FCSTD DOCUMENT  (FreeCAD 0.20R29177 (Git))
Label: AT_900a_GA3Dtech_M1_assembly
License: All rights reserved
LicenseURL: http://en.wikipedia.org/wiki/All_rights_reserved
objects: App::FeaturePython×56, Part::FeaturePython×13, PartDesign::ShapeBinder×6, Sketcher::SketchObject×2, PartDesign::Body×2, PartDesign::AdditivePipe×1, PartDesign::FeatureBase×1
note: 26 computed .brp shape members not serialized (recipe doc carries the construction recipe); baked Part::Feature solids carry a one-line shape summary decoded from their .brp

FEATURE [Part::FeaturePython] b_AQ_901b_Frame_001_  label="AQ_901b_Frame_001"  # a2plus imported part (geometry in sourceFile) (typed FeaturePython)
  a2p_Version = V0.1
  fixedPosition = true
  objectType = a2pPart
  sourceFile = ./AQ_901b_Frame.FCStd
  subassemblyImport = true
  timeLastImport = 1656490796
  updateColors = true
FEATURE [Part::FeaturePython] b_AT_912a_Yaxis_001_  label="AT_912a_Yaxis_001"  # a2plus imported part (geometry in sourceFile) (typed FeaturePython)
  Placement = pos=(100.718,28,161.125) rot=(0,0,1;0rad)
  a2p_Version = V0.1
  fixedPosition = false
  objectType = a2pPart
  sourceFile = ./AT_912a_Yaxis.FCStd
  subassemblyImport = true
  timeLastImport = 1656492010
  updateColors = true
FEATURE [App::FeaturePython] planeCoincident_001  label="planeCoincident_001__AQ_901b_Frame_001"  # a2plus constraint (typed FeaturePython)
  Object1 = b_AT_912a_Yaxis_001_
  Object2 = b_AQ_901b_Frame_001_
  ParentTreeObject = -> b_AT_912a_Yaxis_001_
  SubElement1 = Face1710
  SubElement2 = Face101
  Suppressed = false
  Type = plane
  directionConstraint = 1
  offset = 0
FEATURE [App::FeaturePython] planeCoincident_001_mirror  label="planeCoincident_001__AT_912a_Yaxis_001"  # a2plus constraint (typed FeaturePython)
  Object1 = b_AT_912a_Yaxis_001_
  Object2 = b_AQ_901b_Frame_001_
  ParentTreeObject = -> b_AQ_901b_Frame_001_
  SubElement1 = Face1710
  SubElement2 = Face101
  Suppressed = false
  Type = plane
  directionConstraint = 1
  offset = 0
FEATURE [App::FeaturePython] planeCoincident_002  label="planeCoincident_002__AT_912a_Yaxis_001"  # a2plus constraint (typed FeaturePython)
  Object1 = b_AQ_901b_Frame_001_
  Object2 = b_AT_912a_Yaxis_001_
  ParentTreeObject = -> b_AQ_901b_Frame_001_
  SubElement1 = Face99
  SubElement2 = Face1479
  Suppressed = false
  Type = plane
  directionConstraint = 1
  offset = 6
FEATURE [App::FeaturePython] planeCoincident_002_mirror  label="planeCoincident_002__AQ_901b_Frame_001"  # a2plus constraint (typed FeaturePython)
  Object1 = b_AQ_901b_Frame_001_
  Object2 = b_AT_912a_Yaxis_001_
  ParentTreeObject = -> b_AT_912a_Yaxis_001_
  SubElement1 = Face99
  SubElement2 = Face1479
  Suppressed = false
  Type = plane
  directionConstraint = 1
  offset = 6
FEATURE [Part::FeaturePython] b_AP_982a_DoubleFrontBlocAssembly_001_  label="AP_982a_DoubleFrontBlocAssembly_001"  # a2plus imported part (geometry in sourceFile) (typed FeaturePython)
  Placement = pos=(135.2,436.271,236.375) rot=(1,0,0;1.5708rad)
  a2p_Version = V0.1
  fixedPosition = false
  objectType = a2pPart
  sourceFile = ./AP_982a_DoubleFrontBlocAssembly.FCStd
  subassemblyImport = true
  timeLastImport = 1656489710
  updateColors = true
FEATURE [App::FeaturePython] planeCoincident_003  label="planeCoincident_003__AT_912a_Yaxis_001"  # a2plus constraint (typed FeaturePython)
  Object1 = b_AP_982a_DoubleFrontBlocAssembly_001_
  Object2 = b_AT_912a_Yaxis_001_
  ParentTreeObject = -> b_AP_982a_DoubleFrontBlocAssembly_001_
  SubElement1 = Face1440
  SubElement2 = Face1337
  Suppressed = false
  Type = plane
  directionConstraint = 0
  offset = 0
FEATURE [App::FeaturePython] planeCoincident_003_mirror  label="planeCoincident_003__AP_982a_DoubleFrontBlocAssembly_001"  # a2plus constraint (typed FeaturePython)
  Object1 = b_AP_982a_DoubleFrontBlocAssembly_001_
  Object2 = b_AT_912a_Yaxis_001_
  ParentTreeObject = -> b_AT_912a_Yaxis_001_
  SubElement1 = Face1440
  SubElement2 = Face1337
  Suppressed = false
  Type = plane
  directionConstraint = 0
  offset = 0
FEATURE [App::FeaturePython] planeCoincident_004  label="planeCoincident_004__AQ_901b_Frame_001"  # a2plus constraint (typed FeaturePython)
  Object1 = b_AP_982a_DoubleFrontBlocAssembly_001_
  Object2 = b_AQ_901b_Frame_001_
  ParentTreeObject = -> b_AP_982a_DoubleFrontBlocAssembly_001_
  SubElement1 = Face782
  SubElement2 = Face528
  Suppressed = false
  Type = plane
  directionConstraint = 0
  offset = -1
FEATURE [App::FeaturePython] planeCoincident_004_mirror  label="planeCoincident_004__AP_982a_DoubleFrontBlocAssembly_001"  # a2plus constraint (typed FeaturePython)
  Object1 = b_AP_982a_DoubleFrontBlocAssembly_001_
  Object2 = b_AQ_901b_Frame_001_
  ParentTreeObject = -> b_AQ_901b_Frame_001_
  SubElement1 = Face782
  SubElement2 = Face528
  Suppressed = false
  Type = plane
  directionConstraint = 0
  offset = -1
FEATURE [Part::FeaturePython] b_AT_911a_Xaxis_001_  label="AT_911a_Xaxis_001"  # a2plus imported part (geometry in sourceFile) (typed FeaturePython)
  Placement = pos=(-66.5758,246.062,201.278) rot=(-0.707107,0,-0.707107;3.14159rad)
  a2p_Version = V0.1
  fixedPosition = false
  objectType = a2pPart
  sourceFile = ./AT_911a_Xaxis.FCStd
  subassemblyImport = false
  timeLastImport = 1656491516
  updateColors = true
FEATURE [App::FeaturePython] planeCoincident_005  label="planeCoincident_005__AT_911a_Xaxis_001"  # a2plus constraint (typed FeaturePython)
  Object1 = b_AP_982a_DoubleFrontBlocAssembly_001_
  Object2 = b_AT_911a_Xaxis_001_
  ParentTreeObject = -> b_AP_982a_DoubleFrontBlocAssembly_001_
  SubElement1 = Face60
  SubElement2 = Face13
  Suppressed = false
  Type = plane
  directionConstraint = 0
  offset = -2
FEATURE [App::FeaturePython] planeCoincident_005_mirror  label="planeCoincident_005__AP_982a_DoubleFrontBlocAssembly_001"  # a2plus constraint (typed FeaturePython)
  Object1 = b_AP_982a_DoubleFrontBlocAssembly_001_
  Object2 = b_AT_911a_Xaxis_001_
  ParentTreeObject = -> b_AT_911a_Xaxis_001_
  SubElement1 = Face60
  SubElement2 = Face13
  Suppressed = false
  Type = plane
  directionConstraint = 0
  offset = -2
FEATURE [App::FeaturePython] planeCoincident_006  label="planeCoincident_006__AP_982a_DoubleFrontBlocAssembly_001"  # a2plus constraint (typed FeaturePython)
  Object1 = b_AT_911a_Xaxis_001_
  Object2 = b_AP_982a_DoubleFrontBlocAssembly_001_
  ParentTreeObject = -> b_AT_911a_Xaxis_001_
  SubElement1 = Face15
  SubElement2 = Face56
  Suppressed = false
  Type = plane
  directionConstraint = 0
  offset = 2.8
FEATURE [App::FeaturePython] planeCoincident_006_mirror  label="planeCoincident_006__AT_911a_Xaxis_001"  # a2plus constraint (typed FeaturePython)
  Object1 = b_AT_911a_Xaxis_001_
  Object2 = b_AP_982a_DoubleFrontBlocAssembly_001_
  ParentTreeObject = -> b_AP_982a_DoubleFrontBlocAssembly_001_
  SubElement1 = Face15
  SubElement2 = Face56
  Suppressed = false
  Type = plane
  directionConstraint = 0
  offset = 2.8
FEATURE [Part::FeaturePython] b_AT_913a_Zaxis_001_  label="AT_913a_Zaxis_001"  # a2plus imported part (geometry in sourceFile) (typed FeaturePython)
  Placement = pos=(128.968,435,56.8) rot=(0,0,1;0rad)
  a2p_Version = V0.1
  fixedPosition = false
  objectType = a2pPart
  sourceFile = ./AT_913a_Zaxis.FCStd
  subassemblyImport = false
  timeLastImport = 1656500628
  updateColors = true
FEATURE [App::FeaturePython] planeCoincident_007  label="planeCoincident_007__AQ_901b_Frame_001"  # a2plus constraint (typed FeaturePython)
  Object1 = b_AT_913a_Zaxis_001_
  Object2 = b_AQ_901b_Frame_001_
  ParentTreeObject = -> b_AT_913a_Zaxis_001_
  SubElement1 = Face1362
  SubElement2 = Face24
  Suppressed = false
  Type = plane
  directionConstraint = 0
  offset = 0
FEATURE [App::FeaturePython] planeCoincident_007_mirror  label="planeCoincident_007__AT_913a_Zaxis_001"  # a2plus constraint (typed FeaturePython)
  Object1 = b_AT_913a_Zaxis_001_
  Object2 = b_AQ_901b_Frame_001_
  ParentTreeObject = -> b_AQ_901b_Frame_001_
  SubElement1 = Face1362
  SubElement2 = Face24
  Suppressed = false
  Type = plane
  directionConstraint = 0
  offset = 0
FEATURE [App::FeaturePython] axisCoincident_001  label="axisCoincident_001__AT_912a_Yaxis_001"  # a2plus constraint (typed FeaturePython)
  Object1 = b_AT_913a_Zaxis_001_
  Object2 = b_AT_912a_Yaxis_001_
  ParentTreeObject = -> b_AT_913a_Zaxis_001_
  SubElement1 = Face1
  SubElement2 = Face1445
  Suppressed = false
  Type = axial
  directionConstraint = 1
  lockRotation = false
FEATURE [App::FeaturePython] axisCoincident_001_mirror  label="axisCoincident_001__AT_913a_Zaxis_001"  # a2plus constraint (typed FeaturePython)
  Object1 = b_AT_913a_Zaxis_001_
  Object2 = b_AT_912a_Yaxis_001_
  ParentTreeObject = -> b_AT_912a_Yaxis_001_
  SubElement1 = Face1
  SubElement2 = Face1445
  Suppressed = false
  Type = axial
  directionConstraint = 1
  lockRotation = false
FEATURE [Part::FeaturePython] b_AT_913a_Zaxis_001_001  label="AT_913a_Zaxis_002"  # a2plus imported part (geometry in sourceFile) (typed FeaturePython)
  Placement = pos=(128.968,27,56.8) rot=(0,0,1;0rad)
  a2p_Version = V0.1
  fixedPosition = false
  objectType = a2pPart
  sourceFile = ./AT_913a_Zaxis.FCStd
  subassemblyImport = false
  timeLastImport = 1656500628
  updateColors = true
FEATURE [App::FeaturePython] planeCoincident_008  label="planeCoincident_008__AT_913a_Zaxis_001"  # a2plus constraint (typed FeaturePython)
  Object1 = b_AT_913a_Zaxis_001_001
  Object2 = b_AT_913a_Zaxis_001_
  ParentTreeObject = -> b_AT_913a_Zaxis_001_001
  SubElement1 = Face40
  SubElement2 = Face40
  Suppressed = false
  Type = plane
  directionConstraint = 0
  offset = 0
FEATURE [App::FeaturePython] planeCoincident_008_mirror  label="planeCoincident_008__AT_913a_Zaxis_002"  # a2plus constraint (typed FeaturePython)
  Object1 = b_AT_913a_Zaxis_001_001
  Object2 = b_AT_913a_Zaxis_001_
  ParentTreeObject = -> b_AT_913a_Zaxis_001_
  SubElement1 = Face40
  SubElement2 = Face40
  Suppressed = false
  Type = plane
  directionConstraint = 0
  offset = 0
FEATURE [App::FeaturePython] axisCoincident_002  label="axisCoincident_002__AT_912a_Yaxis_001"  # a2plus constraint (typed FeaturePython)
  Object1 = b_AT_913a_Zaxis_001_001
  Object2 = b_AT_912a_Yaxis_001_
  ParentTreeObject = -> b_AT_913a_Zaxis_001_001
  SubElement1 = Face1
  SubElement2 = Face102
  Suppressed = false
  Type = axial
  directionConstraint = 1
  lockRotation = false
FEATURE [App::FeaturePython] axisCoincident_002_mirror  label="axisCoincident_002__AT_913a_Zaxis_002"  # a2plus constraint (typed FeaturePython)
  Object1 = b_AT_913a_Zaxis_001_001
  Object2 = b_AT_912a_Yaxis_001_
  ParentTreeObject = -> b_AT_912a_Yaxis_001_
  SubElement1 = Face1
  SubElement2 = Face102
  Suppressed = false
  Type = axial
  directionConstraint = 1
  lockRotation = false
FEATURE [Part::FeaturePython] b_AT_920a_ElectroDrawer_assembly_001_  label="AT_920a_ElectroDrawer_assembly_001"  # a2plus imported part (geometry in sourceFile) (typed FeaturePython)
  Placement = pos=(24.1079,349.929,-5.59215) rot=(0,0,1;3.14159rad)
  a2p_Version = V0.1
  fixedPosition = false
  objectType = a2pPart
  sourceFile = ./AT_920a_ElectroDrawer_assembly.FCStd
  subassemblyImport = true
  timeLastImport = 1656503558
  updateColors = true
FEATURE [App::FeaturePython] planeCoincident_009  label="planeCoincident_009__AQ_901b_Frame_001"  # a2plus constraint (typed FeaturePython)
  Object1 = b_AT_920a_ElectroDrawer_assembly_001_
  Object2 = b_AQ_901b_Frame_001_
  ParentTreeObject = -> b_AT_920a_ElectroDrawer_assembly_001_
  SubElement1 = Face4
  SubElement2 = Face1071
  Suppressed = false
  Type = plane
  directionConstraint = 0
  offset = 0
FEATURE [App::FeaturePython] planeCoincident_009_mirror  label="planeCoincident_009__AT_920a_ElectroDrawer_assembly_001"  # a2plus constraint (typed FeaturePython)
  Object1 = b_AT_920a_ElectroDrawer_assembly_001_
  Object2 = b_AQ_901b_Frame_001_
  ParentTreeObject = -> b_AQ_901b_Frame_001_
  SubElement1 = Face4
  SubElement2 = Face1071
  Suppressed = false
  Type = plane
  directionConstraint = 0
  offset = 0
FEATURE [Part::FeaturePython] b_AT_001a_frontfoot_001_  label="AT_001a_frontfoot_001"  # a2plus imported part (geometry in sourceFile) (typed FeaturePython)
  Placement = pos=(-235,55,-10.3002) rot=(0,0,1;0rad)
  a2p_Version = V0.1
  fixedPosition = false
  objectType = a2pPart
  sourceFile = ./AT_001a_frontfoot.FCStd
  subassemblyImport = false
  timeLastImport = 1656508192
  updateColors = true
FEATURE [App::FeaturePython] planeCoincident_010  label="planeCoincident_010__AQ_901b_Frame_001"  # a2plus constraint (typed FeaturePython)
  Object1 = b_AT_001a_frontfoot_001_
  Object2 = b_AQ_901b_Frame_001_
  ParentTreeObject = -> b_AT_001a_frontfoot_001_
  SubElement1 = Face63
  SubElement2 = Face625
  Suppressed = false
  Type = plane
  directionConstraint = 0
  offset = 0
FEATURE [App::FeaturePython] planeCoincident_010_mirror  label="planeCoincident_010__AT_001a_frontfoot_001"  # a2plus constraint (typed FeaturePython)
  Object1 = b_AT_001a_frontfoot_001_
  Object2 = b_AQ_901b_Frame_001_
  ParentTreeObject = -> b_AQ_901b_Frame_001_
  SubElement1 = Face63
  SubElement2 = Face625
  Suppressed = false
  Type = plane
  directionConstraint = 0
  offset = 0
FEATURE [App::FeaturePython] planeCoincident_011  label="planeCoincident_011__AQ_901b_Frame_001"  # a2plus constraint (typed FeaturePython)
  Object1 = b_AT_001a_frontfoot_001_
  Object2 = b_AQ_901b_Frame_001_
  ParentTreeObject = -> b_AT_001a_frontfoot_001_
  SubElement1 = Face19
  SubElement2 = Face622
  Suppressed = false
  Type = plane
  directionConstraint = 0
  offset = 0
FEATURE [App::FeaturePython] planeCoincident_011_mirror  label="planeCoincident_011__AT_001a_frontfoot_001"  # a2plus constraint (typed FeaturePython)
  Object1 = b_AT_001a_frontfoot_001_
  Object2 = b_AQ_901b_Frame_001_
  ParentTreeObject = -> b_AQ_901b_Frame_001_
  SubElement1 = Face19
  SubElement2 = Face622
  Suppressed = false
  Type = plane
  directionConstraint = 0
  offset = 0
FEATURE [App::FeaturePython] planeCoincident_012  label="planeCoincident_012__AQ_901b_Frame_001"  # a2plus constraint (typed FeaturePython)
  Object1 = b_AT_001a_frontfoot_001_
  Object2 = b_AQ_901b_Frame_001_
  ParentTreeObject = -> b_AT_001a_frontfoot_001_
  SubElement1 = Face4
  SubElement2 = Face623
  Suppressed = false
  Type = plane
  directionConstraint = 0
  offset = 0
FEATURE [App::FeaturePython] planeCoincident_012_mirror  label="planeCoincident_012__AT_001a_frontfoot_001"  # a2plus constraint (typed FeaturePython)
  Object1 = b_AT_001a_frontfoot_001_
  Object2 = b_AQ_901b_Frame_001_
  ParentTreeObject = -> b_AQ_901b_Frame_001_
  SubElement1 = Face4
  SubElement2 = Face623
  Suppressed = false
  Type = plane
  directionConstraint = 0
  offset = 0
FEATURE [Part::FeaturePython] b_AT_001a_frontfoot_001_001  label="AT_001a_frontfoot_002"  # a2plus imported part (geometry in sourceFile) (typed FeaturePython)
  Placement = pos=(-235,405,-10.3002) rot=(0,0,1;4.71239rad)
  a2p_Version = V0.1
  fixedPosition = false
  objectType = a2pPart
  sourceFile = ./AT_001a_frontfoot.FCStd
  subassemblyImport = false
  timeLastImport = 1656508192
  updateColors = true
FEATURE [App::FeaturePython] planeCoincident_013  label="planeCoincident_013__AT_001a_frontfoot_001"  # a2plus constraint (typed FeaturePython)
  Object1 = b_AT_001a_frontfoot_001_001
  Object2 = b_AT_001a_frontfoot_001_
  ParentTreeObject = -> b_AT_001a_frontfoot_001_001
  SubElement1 = Face46
  SubElement2 = Face5
  Suppressed = false
  Type = plane
  directionConstraint = 0
  offset = 0
FEATURE [App::FeaturePython] planeCoincident_013_mirror  label="planeCoincident_013__AT_001a_frontfoot_002"  # a2plus constraint (typed FeaturePython)
  Object1 = b_AT_001a_frontfoot_001_001
  Object2 = b_AT_001a_frontfoot_001_
  ParentTreeObject = -> b_AT_001a_frontfoot_001_
  SubElement1 = Face46
  SubElement2 = Face5
  Suppressed = false
  Type = plane
  directionConstraint = 0
  offset = 0
FEATURE [App::FeaturePython] planeCoincident_014  label="planeCoincident_014__AT_001a_frontfoot_001"  # a2plus constraint (typed FeaturePython)
  Object1 = b_AT_001a_frontfoot_001_001
  Object2 = b_AT_001a_frontfoot_001_
  ParentTreeObject = -> b_AT_001a_frontfoot_001_001
  SubElement1 = Face15
  SubElement2 = Face15
  Suppressed = false
  Type = plane
  directionConstraint = 0
  offset = 0
FEATURE [App::FeaturePython] planeCoincident_014_mirror  label="planeCoincident_014__AT_001a_frontfoot_002"  # a2plus constraint (typed FeaturePython)
  Object1 = b_AT_001a_frontfoot_001_001
  Object2 = b_AT_001a_frontfoot_001_
  ParentTreeObject = -> b_AT_001a_frontfoot_001_
  SubElement1 = Face15
  SubElement2 = Face15
  Suppressed = false
  Type = plane
  directionConstraint = 0
  offset = 0
FEATURE [App::FeaturePython] planeCoincident_015  label="planeCoincident_015__AQ_901b_Frame_001"  # a2plus constraint (typed FeaturePython)
  Object1 = b_AT_001a_frontfoot_001_001
  Object2 = b_AQ_901b_Frame_001_
  ParentTreeObject = -> b_AT_001a_frontfoot_001_001
  SubElement1 = Face4
  SubElement2 = Face624
  Suppressed = false
  Type = plane
  directionConstraint = 1
  offset = 0
FEATURE [App::FeaturePython] planeCoincident_015_mirror  label="planeCoincident_015__AT_001a_frontfoot_002"  # a2plus constraint (typed FeaturePython)
  Object1 = b_AT_001a_frontfoot_001_001
  Object2 = b_AQ_901b_Frame_001_
  ParentTreeObject = -> b_AQ_901b_Frame_001_
  SubElement1 = Face4
  SubElement2 = Face624
  Suppressed = false
  Type = plane
  directionConstraint = 1
  offset = 0
FEATURE [PartDesign::ShapeBinder] ShapeBinder
  Placement = pos=(100.709,426.791,210.125) rot=(0.707107,0,0.707107;3.14159rad)
  Support = -> [b_AT_912a_Yaxis_001_]
  TraceSupport = false
FEATURE [PartDesign::ShapeBinder] ShapeBinder001
  Placement = pos=(100.709,35.209,225.625) rot=(0,1,0;3.14159rad)
  Support = -> [b_AT_912a_Yaxis_001_]
  TraceSupport = false
FEATURE [PartDesign::ShapeBinder] ShapeBinder002
  Placement = pos=(72.2,223.271,215.375) rot=(0,0,-1;1.5708rad)
  Support = -> [b_AP_982a_DoubleFrontBlocAssembly_001_]
  TraceSupport = false
FEATURE [PartDesign::ShapeBinder] ShapeBinder003
  Placement = pos=(128.2,269.271,215.375) rot=(0,0,-1;1.5708rad)
  Support = -> [b_AP_982a_DoubleFrontBlocAssembly_001_]
  TraceSupport = false
FEATURE [PartDesign::ShapeBinder] ShapeBinder004
  Placement = pos=(170.883,56.2042,235.65) rot=(0,0.707107,0.707107;3.14159rad)
  Support = -> [b_AT_911a_Xaxis_001_]
  TraceSupport = false
FEATURE [PartDesign::ShapeBinder] ShapeBinder005
  Placement = pos=(95.9651,435.92,235.65) rot=(1,0,0;1.5708rad)
  Support = -> [b_AT_911a_Xaxis_001_]
  TraceSupport = false
FEATURE [Sketcher::SketchObject] Sketch
  ExternalGeometry = -> [ShapeBinder003,ShapeBinder002,ShapeBinder001,ShapeBinder005,ShapeBinder004,ShapeBinder]
  FullyConstrained = false
  MapMode = 5
  Support = -> [XY_Plane]
  sketch-geometry (9):
    g0: ArcOfCircle CenterX=128.2 CenterY=269.271 CenterZ=0 NormalX=0 NormalY=0 NormalZ=1 AngleXU=0 Radius=13 StartAngle=3.16045 EndAngle=4.7433
    g1: ArcOfCircle CenterX=100.709 CenterY=35.209 CenterZ=0 NormalX=0 NormalY=0 NormalZ=1 AngleXU=0 Radius=13 StartAngle=3.19175 EndAngle=6.1989
    g2: LineSegment StartX=333.424 StartY=249.062 StartZ=0 EndX=128.602 EndY=256.277 EndZ=0
    g3: LineSegment StartX=115.202 StartY=269.026 StartZ=0 EndX=106.775 EndY=427.435 EndZ=0
    g4: LineSegment StartX=94.609 StartY=426.791 StartZ=0 EndX=113.663 EndY=34.1146 EndZ=0
    g5: LineSegment StartX=87.7253 StartY=34.5573 StartZ=0 EndX=85.1744 EndY=222.456 EndZ=0
    g6: ArcOfCircle CenterX=100.709 CenterY=426.791 CenterZ=0 NormalX=0 NormalY=0 NormalZ=1 AngleXU=0 Radius=6.1 StartAngle=0.105836 EndAngle=3.1416
    g7: ArcOfCircle CenterX=72.2 CenterY=223.271 CenterZ=0 NormalX=0 NormalY=0 NormalZ=1 AngleXU=0 Radius=13 StartAngle=6.22042 EndAngle=7.83365
    g8: LineSegment StartX=72.4642 StartY=236.268 StartZ=0 EndX=-66.5758 EndY=249.062 EndZ=0
  constraints (18):
    c: Coincident(g0,g-3)
    c: PointOnObject(g0,g-3)
    c: Coincident(g1,g-5)
    c: PointOnObject(g1,g-5)
    c: Coincident(g2,g-6)
    c: Coincident(g2,g0)
    c: Coincident(g3,g0)
    c: Coincident(g4,g1)
    c: Coincident(g5,g1)
    c: Coincident(g6,g-11)
    c: Coincident(g6,g4)
    c: PointOnObject(g6,g-11)
    c: Coincident(g3,g6)
    c: Coincident(g7,g-4)
    c: PointOnObject(g7,g-4)
    c: Coincident(g5,g7)
    c: Coincident(g8,g7)
    c: Coincident(g8,g-10)
FEATURE [Sketcher::SketchObject] Sketch001
  ExternalGeometry = -> [Sketch]
  FullyConstrained = true
  MapMode = 5
  Placement = pos=(0,0,0) rot=(0.57735,0.57735,0.57735;2.0944rad)
  Support = -> [YZ_Plane]
  sketch-geometry (4):
    g0: LineSegment StartX=249.062 StartY=-2.31e-14 StartZ=0 EndX=247.562 EndY=-2.31e-14 EndZ=0
    g1: LineSegment StartX=247.562 StartY=-2.31e-14 StartZ=0 EndX=247.562 EndY=6 EndZ=0
    g2: LineSegment StartX=247.562 StartY=6 StartZ=0 EndX=249.062 EndY=6 EndZ=0
    g3: LineSegment StartX=249.062 StartY=6 StartZ=0 EndX=249.062 EndY=-2.31e-14 EndZ=0
  constraints (11):
    c: Coincident(g0,g1)
    c: Coincident(g1,g2)
    c: Coincident(g2,g3)
    c: Coincident(g3,g0)
    c: Horizontal(g0)
    c: Horizontal(g2)
    c: Vertical(g1)
    c: Vertical(g3)
    c: Coincident(g0,g-3)
    c: DistanceY(g3,g3) = 6
    c: DistanceX(g0,g0) = 1.5
FEATURE [PartDesign::AdditivePipe] AdditivePipe
  AuxilleryCurvelinear = true
  AuxillerySpineTangent = false
  Binormal = (0,0,0)
  Mode = 0
  Placement = pos=(0,0,0) rot=(0.57735,0.57735,0.57735;2.0944rad)
  Profile = -> Sketch001
  Spine = -> Sketch
  SpineTangent = false
  Transformation = 0
  Transition = 0
FEATURE [PartDesign::Body] Body  label="belt_A"
  Group = -> [ShapeBinder,ShapeBinder001,ShapeBinder002,ShapeBinder003,ShapeBinder004,ShapeBinder005,Sketch,Sketch001,AdditivePipe]
  Origin = -> Origin
  Placement = pos=(0,0,215.4) rot=(0,0,1;0rad)
  Tip = -> AdditivePipe
FEATURE [PartDesign::FeatureBase] Clone
  BaseFeature = -> Body
  Placement = pos=(0,0,215.4) rot=(0,0,1;0rad)
FEATURE [PartDesign::Body] Body001  label="belt_B"
  Group = -> [Clone]
  Origin = -> Origin001
  Placement = pos=(0,0,33.3) rot=(0,0,1;0rad)
  Tip = -> Clone
FEATURE [Part::FeaturePython] b_AT_002a_Endswitch_001_  label="AT_002a_Endswitch_001"  # a2plus imported part (geometry in sourceFile) (typed FeaturePython)
  Placement = pos=(181.15,256.912,232.625) rot=(-0.57735,-0.57735,0.57735;2.0944rad)
  a2p_Version = V0.1
  fixedPosition = false
  objectType = a2pPart
  sourceFile = ./AT_002a_Endswitch.FCStd
  subassemblyImport = false
  timeLastImport = 1656515072
  updateColors = true
FEATURE [App::FeaturePython] planeCoincident_016  label="planeCoincident_016__AP_982a_DoubleFrontBlocAssembly_001"  # a2plus constraint (typed FeaturePython)
  Object1 = b_AT_002a_Endswitch_001_
  Object2 = b_AP_982a_DoubleFrontBlocAssembly_001_
  ParentTreeObject = -> b_AT_002a_Endswitch_001_
  SubElement1 = Face70
  SubElement2 = Face1
  Suppressed = false
  Type = plane
  directionConstraint = 1
  offset = 0
FEATURE [App::FeaturePython] planeCoincident_016_mirror  label="planeCoincident_016__AT_002a_Endswitch_001"  # a2plus constraint (typed FeaturePython)
  Object1 = b_AT_002a_Endswitch_001_
  Object2 = b_AP_982a_DoubleFrontBlocAssembly_001_
  ParentTreeObject = -> b_AP_982a_DoubleFrontBlocAssembly_001_
  SubElement1 = Face70
  SubElement2 = Face1
  Suppressed = false
  Type = plane
  directionConstraint = 1
  offset = 0
FEATURE [App::FeaturePython] planeCoincident_017  label="planeCoincident_017__AP_982a_DoubleFrontBlocAssembly_001"  # a2plus constraint (typed FeaturePython)
  Object1 = b_AT_002a_Endswitch_001_
  Object2 = b_AP_982a_DoubleFrontBlocAssembly_001_
  ParentTreeObject = -> b_AT_002a_Endswitch_001_
  SubElement1 = Face59
  SubElement2 = Face2
  Suppressed = false
  Type = plane
  directionConstraint = 0
  offset = 0
FEATURE [App::FeaturePython] planeCoincident_017_mirror  label="planeCoincident_017__AT_002a_Endswitch_001"  # a2plus constraint (typed FeaturePython)
  Object1 = b_AT_002a_Endswitch_001_
  Object2 = b_AP_982a_DoubleFrontBlocAssembly_001_
  ParentTreeObject = -> b_AP_982a_DoubleFrontBlocAssembly_001_
  SubElement1 = Face59
  SubElement2 = Face2
  Suppressed = false
  Type = plane
  directionConstraint = 0
  offset = 0
FEATURE [App::FeaturePython] planeCoincident_018  label="planeCoincident_018__AT_911a_Xaxis_001"  # a2plus constraint (typed FeaturePython)
  Object1 = b_AT_002a_Endswitch_001_
  Object2 = b_AT_911a_Xaxis_001_
  ParentTreeObject = -> b_AT_002a_Endswitch_001_
  SubElement1 = Face288
  SubElement2 = Face188
  Suppressed = false
  Type = plane
  directionConstraint = 1
  offset = 0
FEATURE [App::FeaturePython] planeCoincident_018_mirror  label="planeCoincident_018__AT_002a_Endswitch_001"  # a2plus constraint (typed FeaturePython)
  Object1 = b_AT_002a_Endswitch_001_
  Object2 = b_AT_911a_Xaxis_001_
  ParentTreeObject = -> b_AT_911a_Xaxis_001_
  SubElement1 = Face288
  SubElement2 = Face188
  Suppressed = false
  Type = plane
  directionConstraint = 1
  offset = 0
FEATURE [Part::FeaturePython] b_AT_002a_Endswitch_001_001  label="AT_002a_Endswitch_002"  # a2plus imported part (geometry in sourceFile) (typed FeaturePython)
  Placement = pos=(168.95,304.221,250.385) rot=(0,0.707107,-0.707107;3.14159rad)
  a2p_Version = V0.1
  fixedPosition = false
  objectType = a2pPart
  sourceFile = ./AT_002a_Endswitch.FCStd
  subassemblyImport = false
  timeLastImport = 1656515072
  updateColors = true
FEATURE [App::FeaturePython] planeCoincident_019  label="planeCoincident_019__AP_982a_DoubleFrontBlocAssembly_001"  # a2plus constraint (typed FeaturePython)
  Object1 = b_AT_002a_Endswitch_001_001
  Object2 = b_AP_982a_DoubleFrontBlocAssembly_001_
  ParentTreeObject = -> b_AT_002a_Endswitch_001_001
  SubElement1 = Face666
  SubElement2 = Face44
  Suppressed = false
  Type = plane
  directionConstraint = 1
  offset = 0
FEATURE [App::FeaturePython] planeCoincident_019_mirror  label="planeCoincident_019__AT_002a_Endswitch_002"  # a2plus constraint (typed FeaturePython)
  Object1 = b_AT_002a_Endswitch_001_001
  Object2 = b_AP_982a_DoubleFrontBlocAssembly_001_
  ParentTreeObject = -> b_AP_982a_DoubleFrontBlocAssembly_001_
  SubElement1 = Face666
  SubElement2 = Face44
  Suppressed = false
  Type = plane
  directionConstraint = 1
  offset = 0
FEATURE [App::FeaturePython] planeCoincident_020  label="planeCoincident_020__AP_982a_DoubleFrontBlocAssembly_001"  # a2plus constraint (typed FeaturePython)
  Object1 = b_AT_002a_Endswitch_001_001
  Object2 = b_AP_982a_DoubleFrontBlocAssembly_001_
  ParentTreeObject = -> b_AT_002a_Endswitch_001_001
  SubElement1 = Face70
  SubElement2 = Face82
  Suppressed = false
  Type = plane
  directionConstraint = 0
  offset = 0
FEATURE [App::FeaturePython] planeCoincident_020_mirror  label="planeCoincident_020__AT_002a_Endswitch_002"  # a2plus constraint (typed FeaturePython)
  Object1 = b_AT_002a_Endswitch_001_001
  Object2 = b_AP_982a_DoubleFrontBlocAssembly_001_
  ParentTreeObject = -> b_AP_982a_DoubleFrontBlocAssembly_001_
  SubElement1 = Face70
  SubElement2 = Face82
  Suppressed = false
  Type = plane
  directionConstraint = 0
  offset = 0
FEATURE [App::FeaturePython] planeCoincident_021  label="planeCoincident_021__AP_982a_DoubleFrontBlocAssembly_001"  # a2plus constraint (typed FeaturePython)
  Object1 = b_AT_002a_Endswitch_001_001
  Object2 = b_AP_982a_DoubleFrontBlocAssembly_001_
  ParentTreeObject = -> b_AT_002a_Endswitch_001_001
  SubElement1 = Face41
  SubElement2 = Face1
  Suppressed = false
  Type = plane
  directionConstraint = 1
  offset = 0
FEATURE [App::FeaturePython] planeCoincident_021_mirror  label="planeCoincident_021__AT_002a_Endswitch_002"  # a2plus constraint (typed FeaturePython)
  Object1 = b_AT_002a_Endswitch_001_001
  Object2 = b_AP_982a_DoubleFrontBlocAssembly_001_
  ParentTreeObject = -> b_AP_982a_DoubleFrontBlocAssembly_001_
  SubElement1 = Face41
  SubElement2 = Face1
  Suppressed = false
  Type = plane
  directionConstraint = 1
  offset = 0
FEATURE [Part::FeaturePython] b_AT_002a_Endswitch_001_002  label="AT_002a_Endswitch_003"  # a2plus imported part (geometry in sourceFile) (typed FeaturePython)
  Placement = pos=(67.83,435.25,30.85) rot=(-1,0,0;3.14159rad)
  a2p_Version = V0.1
  fixedPosition = false
  objectType = a2pPart
  sourceFile = ./AT_002a_Endswitch.FCStd
  subassemblyImport = false
  timeLastImport = 1656515072
  updateColors = true
FEATURE [App::FeaturePython] planeCoincident_022  label="planeCoincident_022__AQ_901b_Frame_001"  # a2plus constraint (typed FeaturePython)
  Object1 = b_AT_002a_Endswitch_001_002
  Object2 = b_AQ_901b_Frame_001_
  ParentTreeObject = -> b_AT_002a_Endswitch_001_002
  SubElement1 = Face37
  SubElement2 = Face24
  Suppressed = false
  Type = plane
  directionConstraint = 0
  offset = 0
FEATURE [App::FeaturePython] planeCoincident_022_mirror  label="planeCoincident_022__AT_002a_Endswitch_003"  # a2plus constraint (typed FeaturePython)
  Object1 = b_AT_002a_Endswitch_001_002
  Object2 = b_AQ_901b_Frame_001_
  ParentTreeObject = -> b_AQ_901b_Frame_001_
  SubElement1 = Face37
  SubElement2 = Face24
  Suppressed = false
  Type = plane
  directionConstraint = 0
  offset = 0
FEATURE [App::FeaturePython] planeCoincident_023  label="planeCoincident_023__AT_002a_Endswitch_003"  # a2plus constraint (typed FeaturePython)
  Object1 = b_AT_913a_Zaxis_001_
  Object2 = b_AT_002a_Endswitch_001_002
  ParentTreeObject = -> b_AT_913a_Zaxis_001_
  SubElement1 = Face1342
  SubElement2 = Face364
  Suppressed = false
  Type = plane
  directionConstraint = 0
  offset = -10
FEATURE [App::FeaturePython] planeCoincident_023_mirror  label="planeCoincident_023__AT_913a_Zaxis_001"  # a2plus constraint (typed FeaturePython)
  Object1 = b_AT_913a_Zaxis_001_
  Object2 = b_AT_002a_Endswitch_001_002
  ParentTreeObject = -> b_AT_002a_Endswitch_001_002
  SubElement1 = Face1342
  SubElement2 = Face364
  Suppressed = false
  Type = plane
  directionConstraint = 0
  offset = -10
FEATURE [App::FeaturePython] planeCoincident_024  label="planeCoincident_024__AQ_901b_Frame_001"  # a2plus constraint (typed FeaturePython)
  Object1 = b_AT_002a_Endswitch_001_002
  Object2 = b_AQ_901b_Frame_001_
  ParentTreeObject = -> b_AT_002a_Endswitch_001_002
  SubElement1 = Face59
  SubElement2 = Face13
  Suppressed = false
  Type = plane
  directionConstraint = 1
  offset = 0
FEATURE [App::FeaturePython] planeCoincident_024_mirror  label="planeCoincident_024__AT_002a_Endswitch_003"  # a2plus constraint (typed FeaturePython)
  Object1 = b_AT_002a_Endswitch_001_002
  Object2 = b_AQ_901b_Frame_001_
  ParentTreeObject = -> b_AQ_901b_Frame_001_
  SubElement1 = Face59
  SubElement2 = Face13
  Suppressed = false
  Type = plane
  directionConstraint = 1
  offset = 0
FEATURE [Part::FeaturePython] b_AT_003a_touchprobeZ_001_  label="AT_003a_touchprobeZ_001"  # a2plus imported part (geometry in sourceFile) (typed FeaturePython)
  Placement = pos=(144.63,901,-4.99798) rot=(0,0,1;3.14159rad)
  a2p_Version = V0.1
  fixedPosition = false
  objectType = a2pPart
  sourceFile = ./AT_003a_touchprobeZ.FCStd
  subassemblyImport = false
  timeLastImport = 1656516756
  updateColors = true
FEATURE [App::FeaturePython] planeCoincident_025  label="planeCoincident_025__AT_912a_Yaxis_001"  # a2plus constraint (typed FeaturePython)
  Object1 = b_AT_003a_touchprobeZ_001_
  Object2 = b_AT_912a_Yaxis_001_
  ParentTreeObject = -> b_AT_003a_touchprobeZ_001_
  SubElement1 = Face5
  SubElement2 = Face1872
  Suppressed = false
  Type = plane
  directionConstraint = 1
  offset = 0
FEATURE [App::FeaturePython] planeCoincident_025_mirror  label="planeCoincident_025__AT_003a_touchprobeZ_001"  # a2plus constraint (typed FeaturePython)
  Object1 = b_AT_003a_touchprobeZ_001_
  Object2 = b_AT_912a_Yaxis_001_
  ParentTreeObject = -> b_AT_912a_Yaxis_001_
  SubElement1 = Face5
  SubElement2 = Face1872
  Suppressed = false
  Type = plane
  directionConstraint = 1
  offset = 0
FEATURE [App::FeaturePython] planeCoincident_026  label="planeCoincident_026__AT_912a_Yaxis_001"  # a2plus constraint (typed FeaturePython)
  Object1 = b_AT_003a_touchprobeZ_001_
  Object2 = b_AT_912a_Yaxis_001_
  ParentTreeObject = -> b_AT_003a_touchprobeZ_001_
  SubElement1 = Face1
  SubElement2 = Face1539
  Suppressed = false
  Type = plane
  directionConstraint = 1
  offset = -30
FEATURE [App::FeaturePython] planeCoincident_026_mirror  label="planeCoincident_026__AT_003a_touchprobeZ_001"  # a2plus constraint (typed FeaturePython)
  Object1 = b_AT_003a_touchprobeZ_001_
  Object2 = b_AT_912a_Yaxis_001_
  ParentTreeObject = -> b_AT_912a_Yaxis_001_
  SubElement1 = Face1
  SubElement2 = Face1539
  Suppressed = false
  Type = plane
  directionConstraint = 1
  offset = -30
